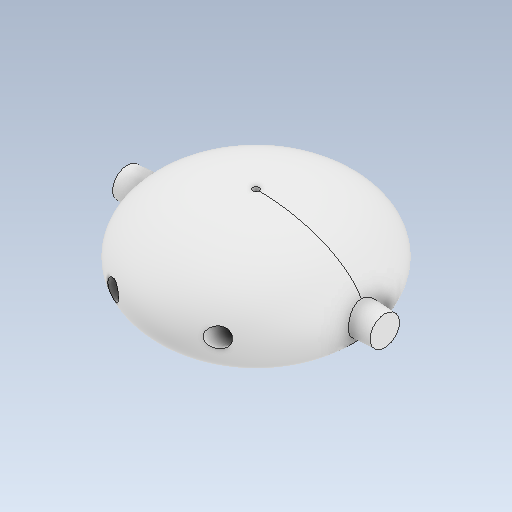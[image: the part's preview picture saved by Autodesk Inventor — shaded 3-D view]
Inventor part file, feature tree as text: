
AUTODESK INVENTOR PART (.ipt)
format: ipt  version: 2021 (Build 250183000, 183)  size: 295,936 bytes
history: native  units: mm
features: other x3, sketch x3
ambient origin geometry x8: Origin, YZ Plane, XZ Plane, XY Plane, X Axis, Y Axis, Z Axis, Center Point
bodies: Solid1 (feature_tree)
feature tree (6):
  other  "head final.ipt"
  other  "Solid1::head final.ipt"
  other  "TaggingFeature1"
  sketch  "Sketch4"  dims[d0=30.0mm]
  sketch  "Sketch8"
  sketch  "Sketch9"
